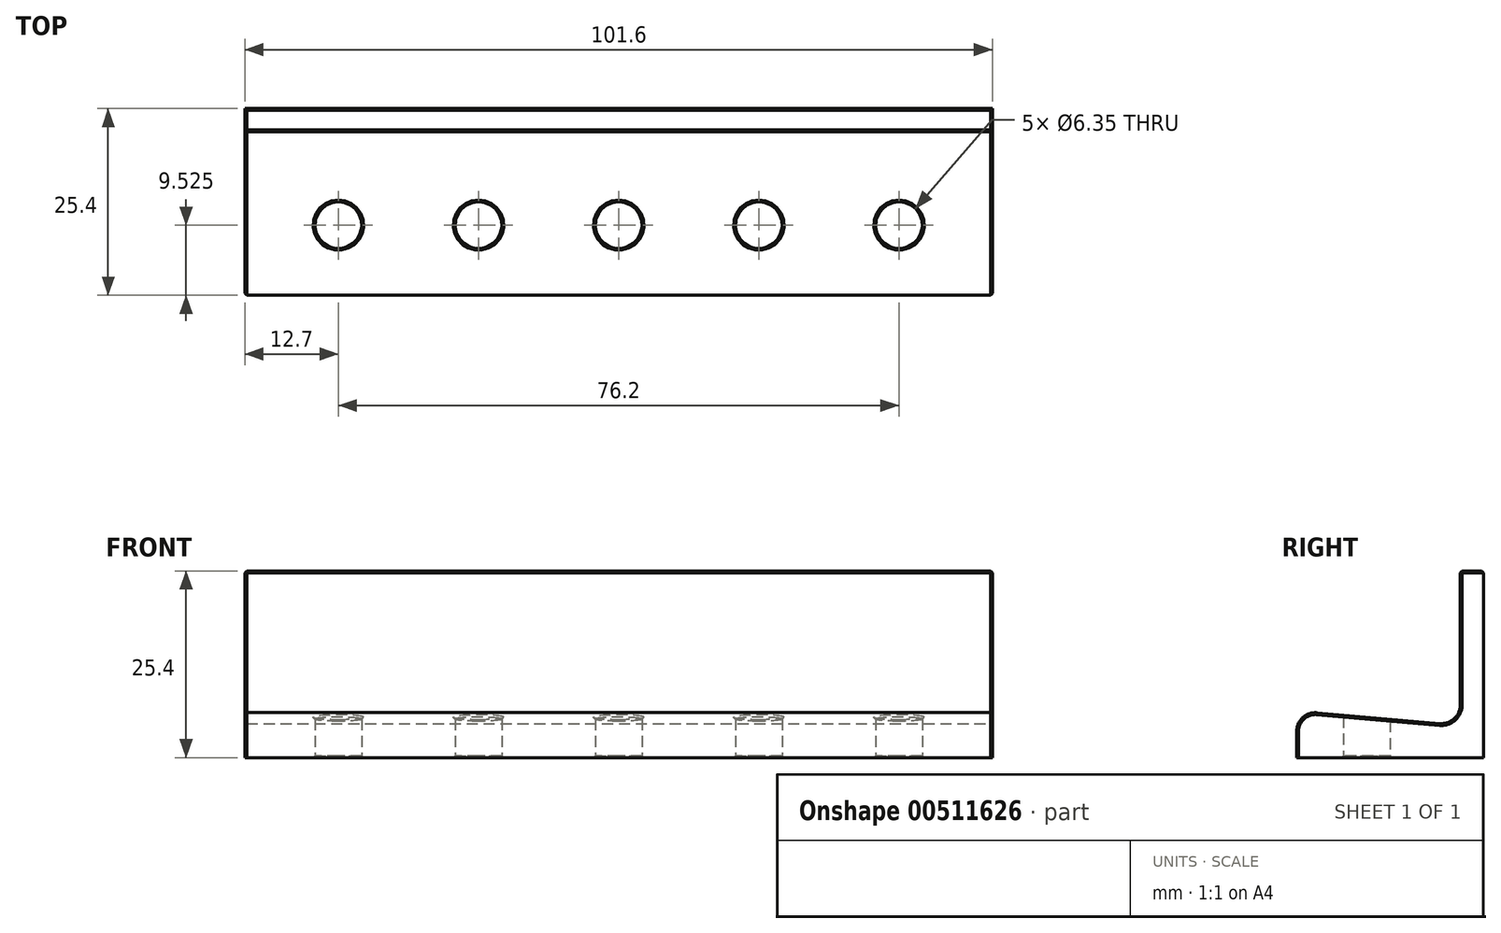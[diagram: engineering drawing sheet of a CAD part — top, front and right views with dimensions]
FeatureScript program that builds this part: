
annotation { "Feature Type Name" : "Feature", "Feature Type Description" : "" }
export const myFeature = defineFeature(function(context is Context, id is Id, definition is map)
    precondition{}
    {
        {
            var Q0;
            Q0=qCreatedBy(makeId("Front.planeOp"),FACE);
            var sketch = newSketch(context, id + "F0", { "sketchPlane" : qUnion([Q0])});
            skLineSegment(sketch, "E0.bottom", {"start": v(-50.8, 25.4) * mm, "end": v(50.8, 25.4) * mm});
            skLineSegment(sketch, "E0.top", {"start": v(-50.8, 0) * mm, "end": v(50.8, 0) * mm});
            skLineSegment(sketch, "E0.left", {"start": v(-50.8, 25.4) * mm, "end": v(-50.8, 0) * mm});
            skLineSegment(sketch, "E0.right", {"start": v(50.8, 25.4) * mm, "end": v(50.8, 0) * mm});
            skSolve(sketch);
        }
        {
            var Q0;
            Q0=qCreatedBy(makeId("Top.planeOp"),FACE);
            var sketch = newSketch(context, id + "F1", { "sketchPlane" : qUnion([Q0])});
            skLineSegment(sketch, "E1.bottom", {"start": v(-50.8, -25.4) * mm, "end": v(50.8, -25.4) * mm});
            skLineSegment(sketch, "E1.top", {"start": v(-50.8, 0) * mm, "end": v(50.8, 0) * mm});
            skLineSegment(sketch, "E1.left", {"start": v(-50.8, -25.4) * mm, "end": v(-50.8, 0) * mm});
            skLineSegment(sketch, "E1.right", {"start": v(50.8, -25.4) * mm, "end": v(50.8, 0) * mm});
            skCircle(sketch, "E2", {"center": v(-38.1, -15.87) * mm, "radius": 3.18 * mm});
            skCircle(sketch, "E3.1.0.0", {"center": v(-19.05, -15.87) * mm, "radius": 3.18 * mm});
            skCircle(sketch, "E3.2.0.0", {"center": v(0, -15.88) * mm, "radius": 3.18 * mm});
            skCircle(sketch, "E3.3.0.0", {"center": v(19.05, -15.88) * mm, "radius": 3.18 * mm});
            skCircle(sketch, "E3.4.0.0", {"center": v(38.1, -15.88) * mm, "radius": 3.18 * mm});
            skLineSegment(sketch, "E3.direction1", {"start": v(-38.1, -15.87) * mm, "end": v(-19.05, -15.87) * mm, "construction": true});
            skLineSegment(sketch, "E4", {"start": v(0, 0) * mm, "end": v(0, -49.19) * mm, "construction": true});
            skSolve(sketch);
        }
        {
            var Q0;
            Q0=makeQuery(id+"F0.imprint","IMPRINT",FACE,{"disambiguationData":[TD([[makeQuery(id+"F0.imprint","IMPRINT",EDGE,{"derivedFrom":sQuery(id+"F0.wireOp",EDGE,"E0.bottom")}),-1.0]])]});
            extrude(context, id + "F2", {"entities" : qUnion([Q0]), "depth" : 3.17 * mm});
        }
        {
            var Q0;
            Q0=qCreatedBy(makeId("Right.planeOp"),FACE);
            var sketch = newSketch(context, id + "F3", { "sketchPlane" : qUnion([Q0])});
            skLineSegment(sketch, "E5.bottom", {"start": v(-25.4, 6.35) * mm, "end": v(0, 4.13) * mm});
            skLineSegment(sketch, "E5.top", {"start": v(-25.4, 0) * mm, "end": v(0, 0) * mm});
            skLineSegment(sketch, "E5.left", {"start": v(-25.4, 6.35) * mm, "end": v(-25.4, 0) * mm});
            skLineSegment(sketch, "E5.right", {"start": v(0, 4.13) * mm, "end": v(0, 0) * mm});
            skLineSegment(sketch, "E6", {"start": v(0, 0) * mm, "end": v(-25.4, 0) * mm});
            skSolve(sketch);
        }
        {
            var Q0;
            Q0=sQuery(id+"F3.wireOp",EDGE,"E5.bottom");
            extrude(context, id + "F4", {"bodyType" : ToolBodyType.SURFACE, "operationType" : NewBodyOperationType.INTERSECT, "surfaceEntities" : qUnion([Q0]), "endBound" : BoundingType.SYMMETRIC, "depth" : 121.92 * mm});
        }
        {
            var Q0;
            Q0=makeQuery(id+"F1.imprint","IMPRINT",FACE,{"disambiguationData":[TD([[makeQuery(id+"F1.imprint","IMPRINT",EDGE,{"derivedFrom":sQuery(id+"F1.wireOp",EDGE,"E1.bottom")}),1.0]])]});
            var Q1;
            Q1=makeQuery(id+"F4.opExtrude","SWEPT_FACE",FACE,{"disambiguationData":[OSD([sQuery(id+"F3.wireOp",EDGE,"E5.bottom")])]});
            extrude(context, id + "F5", {"entities" : qUnion([Q0]), "operationType" : NewBodyOperationType.ADD, "endBound" : BoundingType.UP_TO_SURFACE, "endBoundEntityFace" : qUnion([Q1]), "depth" : 6.35 * mm});
        }
        {
            var Q0;
            Q0=makeQuery(id+"F5.opExtrude","CAP_EDGE",EDGE,{"disambiguationData":[OSD([sQuery(id+"F1.wireOp",EDGE,"E1.bottom")])],"isStart":false});
            fillet(context, id + "F6", {"entities" : qUnion([Q0]), "radius" : 2.54 * mm, "tangentPropagation" : true, "allowEdgeOverflow" : false});
        }
        {
            var Q0;
            Q0=makeQuery(id+"F5.boolean.opBoolean","INTERSECT",EDGE,{"derivedFrom":[makeQuery(id+"F2.opExtrude","CAP_FACE",FACE,{"disambiguationData":[OSD([sQuery(id+"F0.wireOp",EDGE,"E0.bottom"),sQuery(id+"F0.wireOp",EDGE,"E0.top"),sQuery(id+"F0.wireOp",EDGE,"E0.left"),sQuery(id+"F0.wireOp",EDGE,"E0.right")])],"isStart":false}),makeQuery(id+"F5.opExtrude","CAP_FACE",FACE,{"disambiguationData":[OSD([sQuery(id+"F1.wireOp",EDGE,"E1.bottom"),sQuery(id+"F1.wireOp",EDGE,"E1.top"),sQuery(id+"F1.wireOp",EDGE,"E1.left"),sQuery(id+"F1.wireOp",EDGE,"E1.right"),sQuery(id+"F1.wireOp",EDGE,"E2"),sQuery(id+"F1.wireOp",EDGE,"E3.1.0.0"),sQuery(id+"F1.wireOp",EDGE,"E3.2.0.0"),sQuery(id+"F1.wireOp",EDGE,"E3.3.0.0"),sQuery(id+"F1.wireOp",EDGE,"E3.4.0.0")])],"isStart":false})]});
            fillet(context, id + "F7", {"entities" : qUnion([Q0]), "radius" : 2.54 * mm, "tangentPropagation" : true, "allowEdgeOverflow" : false});
        }
        {
            var Q0;
            Q0=makeQuery(id+"F5.opExtrude","CAP_EDGE",EDGE,{"disambiguationData":[OSD([sQuery(id+"F1.wireOp",EDGE,"E1.left")])],"isStart":false});
            var Q1;
            Q1=makeQuery(id+"F2.opExtrude","CAP_EDGE",EDGE,{"disambiguationData":[OSD([sQuery(id+"F0.wireOp",EDGE,"E0.left")])],"isStart":false});
            var Q2;
            Q2=makeQuery(id+"F2.opExtrude","SWEPT_FACE",FACE,{"disambiguationData":[OSD([sQuery(id+"F0.wireOp",EDGE,"E0.bottom")])]});
            var Q3;
            Q3=makeQuery(id+"F5.opExtrude","CAP_EDGE",EDGE,{"disambiguationData":[OSD([sQuery(id+"F1.wireOp",EDGE,"E1.right")])],"isStart":false});
            var Q4;
            Q4=makeQuery(id+"F2.opExtrude","CAP_EDGE",EDGE,{"disambiguationData":[OSD([sQuery(id+"F0.wireOp",EDGE,"E0.right")])],"isStart":false});
            var Q5;
            Q5=makeQuery(id+"F5.opExtrude","CAP_EDGE",EDGE,{"disambiguationData":[OSD([sQuery(id+"F1.wireOp",EDGE,"E2")])],"isStart":false});
            var Q6;
            Q6=makeQuery(id+"F5.opExtrude","CAP_EDGE",EDGE,{"disambiguationData":[OSD([sQuery(id+"F1.wireOp",EDGE,"E3.1.0.0")])],"isStart":false});
            var Q7;
            Q7=makeQuery(id+"F5.opExtrude","CAP_EDGE",EDGE,{"disambiguationData":[OSD([sQuery(id+"F1.wireOp",EDGE,"E3.2.0.0")])],"isStart":false});
            var Q8;
            Q8=makeQuery(id+"F5.opExtrude","CAP_EDGE",EDGE,{"disambiguationData":[OSD([sQuery(id+"F1.wireOp",EDGE,"E3.3.0.0")])],"isStart":false});
            var Q9;
            Q9=makeQuery(id+"F5.opExtrude","CAP_EDGE",EDGE,{"disambiguationData":[OSD([sQuery(id+"F1.wireOp",EDGE,"E3.4.0.0")])],"isStart":false});
            var Q10;
            Q10=makeQuery(id+"F5.opExtrude","CAP_EDGE",EDGE,{"disambiguationData":[OSD([sQuery(id+"F1.wireOp",EDGE,"E2")])],"isStart":true});
            var Q11;
            Q11=makeQuery(id+"F5.opExtrude","CAP_EDGE",EDGE,{"disambiguationData":[OSD([sQuery(id+"F1.wireOp",EDGE,"E3.1.0.0")])],"isStart":true});
            var Q12;
            Q12=makeQuery(id+"F5.opExtrude","CAP_EDGE",EDGE,{"disambiguationData":[OSD([sQuery(id+"F1.wireOp",EDGE,"E3.2.0.0")])],"isStart":true});
            var Q13;
            Q13=makeQuery(id+"F5.opExtrude","CAP_EDGE",EDGE,{"disambiguationData":[OSD([sQuery(id+"F1.wireOp",EDGE,"E3.3.0.0")])],"isStart":true});
            var Q14;
            Q14=makeQuery(id+"F5.opExtrude","CAP_EDGE",EDGE,{"disambiguationData":[OSD([sQuery(id+"F1.wireOp",EDGE,"E3.4.0.0")])],"isStart":true});
            chamfer(context, id + "F8", {"entities" : qUnion([Q0, Q1, Q2, Q3, Q4, Q5, Q6, Q7, Q8, Q9, Q10, Q11, Q12, Q13, Q14]), "width" : 0.25 * mm, "tangentPropagation" : true});
        }
        {
            var Q0;
            Q0=makeQuery(id+"F4.opExtrude","SWEPT_BODY",BODY,{"disambiguationData":[OSD([sQuery(id+"F3.wireOp",EDGE,"E5.bottom")])]});
            deleteBodies(context, id + "F9", {"entities" : qUnion([Q0])});
        }
    });
